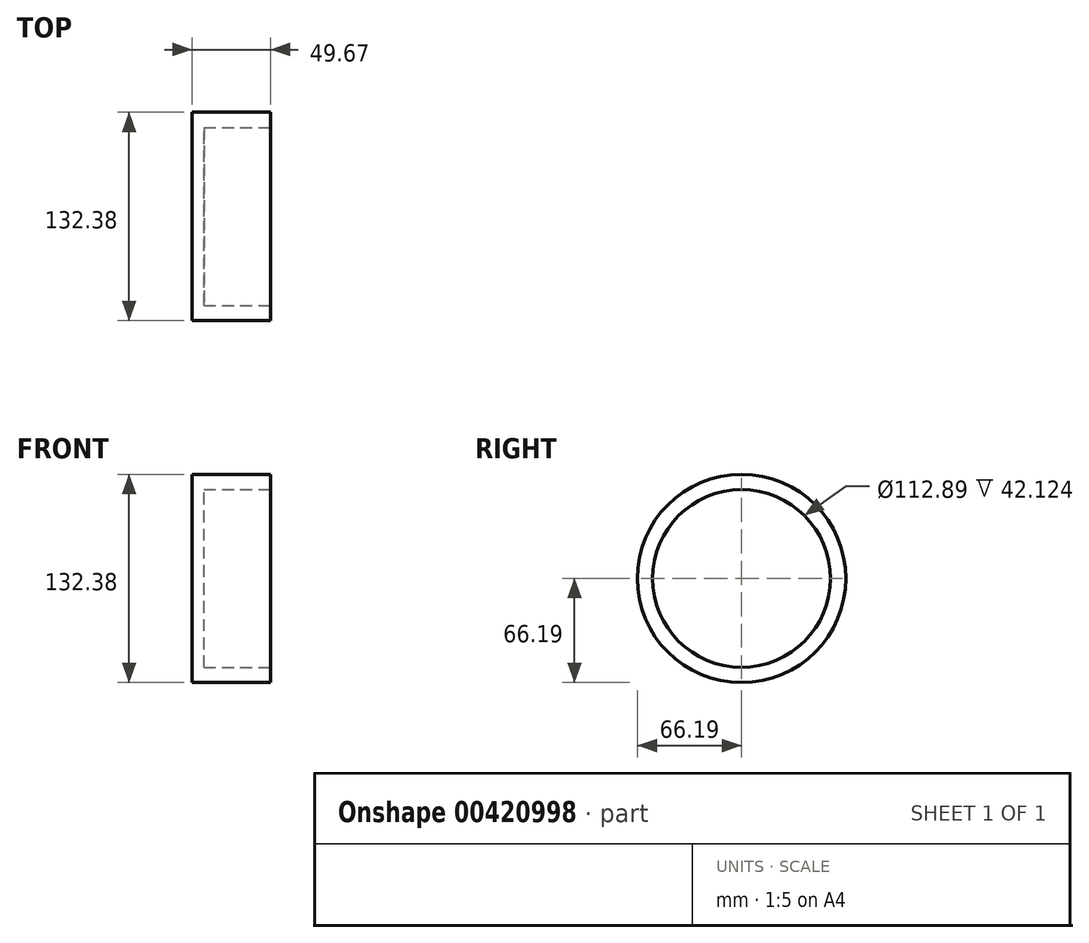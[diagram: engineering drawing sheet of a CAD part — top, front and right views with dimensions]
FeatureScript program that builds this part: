
annotation { "Feature Type Name" : "Feature", "Feature Type Description" : "" }
export const myFeature = defineFeature(function(context is Context, id is Id, definition is map)
    precondition{}
    {
        {
            var Q0;
            Q0=qCreatedBy(makeId("Front.planeOp"),FACE);
            var sketch = newSketch(context, id + "F0", { "sketchPlane" : qUnion([Q0])});
            skLineSegment(sketch, "E0", {"start": v(0, 0) * mm, "end": v(0, 66.19) * mm});
            skLineSegment(sketch, "E1", {"start": v(0, 66.19) * mm, "end": v(49.67, 66.19) * mm});
            skLineSegment(sketch, "E2", {"start": v(49.67, 66.19) * mm, "end": v(49.67, 56.44) * mm});
            skLineSegment(sketch, "E3", {"start": v(49.67, 56.44) * mm, "end": v(7.55, 56.44) * mm});
            skLineSegment(sketch, "E4", {"start": v(7.55, 56.44) * mm, "end": v(7.55, 0) * mm});
            skLineSegment(sketch, "E5", {"start": v(7.55, 0) * mm, "end": v(0, 0) * mm});
            skSolve(sketch);
        }
        {
            var Q0;
            Q0=makeQuery(id+"F0.imprint","IMPRINT",FACE,{"disambiguationData":[TD([[makeQuery(id+"F0.imprint","IMPRINT",EDGE,{"derivedFrom":sQuery(id+"F0.wireOp",EDGE,"E0")}),-1.0]])]});
            var Q1;
            Q1=sQuery(id+"F0.wireOp",EDGE,"E5");
            revolve(context, id + "F1", {"entities" : qUnion([Q0]), "axis" : qUnion([Q1]), "revolveType" : RevolveType.FULL});
        }
    });
